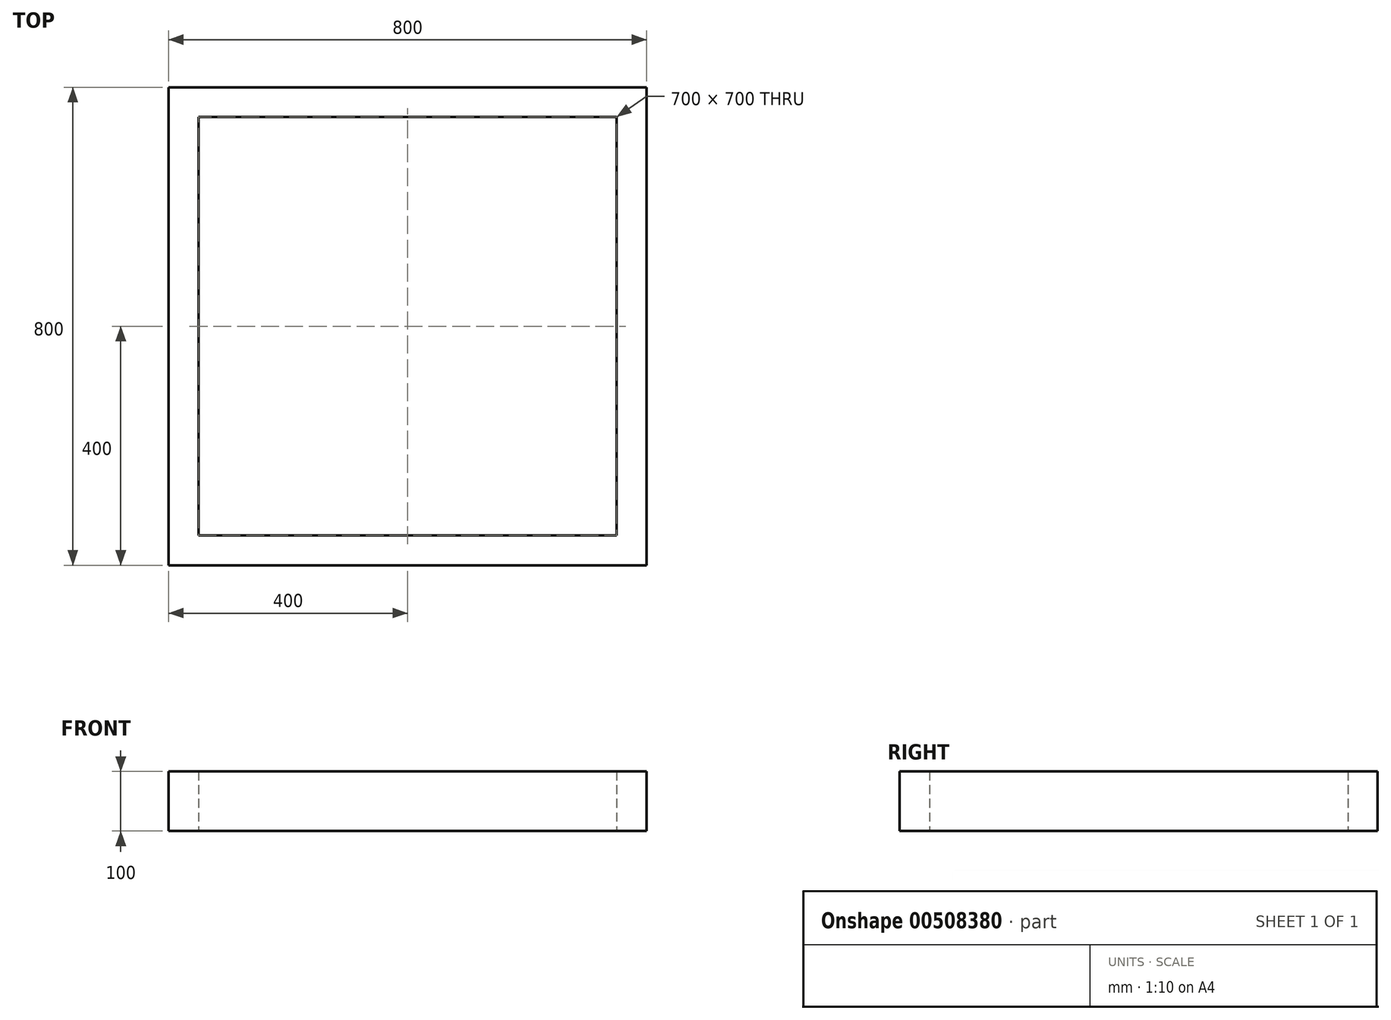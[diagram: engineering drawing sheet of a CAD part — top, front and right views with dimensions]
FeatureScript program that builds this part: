
annotation { "Feature Type Name" : "Feature", "Feature Type Description" : "" }
export const myFeature = defineFeature(function(context is Context, id is Id, definition is map)
    precondition{}
    {
        {
            var Q0;
            Q0=qCreatedBy(makeId("Top.planeOp"),FACE);
            var sketch = newSketch(context, id + "F0", { "sketchPlane" : qUnion([Q0])});
            skLineSegment(sketch, "E0.bottom", {"start": v(400, -400) * mm, "end": v(-400, -400) * mm});
            skLineSegment(sketch, "E0.top", {"start": v(400, 400) * mm, "end": v(-400, 400) * mm});
            skLineSegment(sketch, "E0.left", {"start": v(400, -400) * mm, "end": v(400, 400) * mm});
            skLineSegment(sketch, "E0.right", {"start": v(-400, -400) * mm, "end": v(-400, 400) * mm});
            skPoint(sketch, "E0.middle", {"position": v(0, 0) * mm});
            skLineSegment(sketch, "E1.bottom", {"start": v(350, -350) * mm, "end": v(-350, -350) * mm});
            skLineSegment(sketch, "E1.top", {"start": v(350, 350) * mm, "end": v(-350, 350) * mm});
            skLineSegment(sketch, "E1.left", {"start": v(350, -350) * mm, "end": v(350, 350) * mm});
            skLineSegment(sketch, "E1.right", {"start": v(-350, -350) * mm, "end": v(-350, 350) * mm});
            skSolve(sketch);
        }
        {
            var Q0;
            Q0 = qSketchRegion(id + "F0", true);
            extrude(context, id + "F1", {"entities" : qUnion([Q0]), "depth" : 100 * mm});
        }
    });
